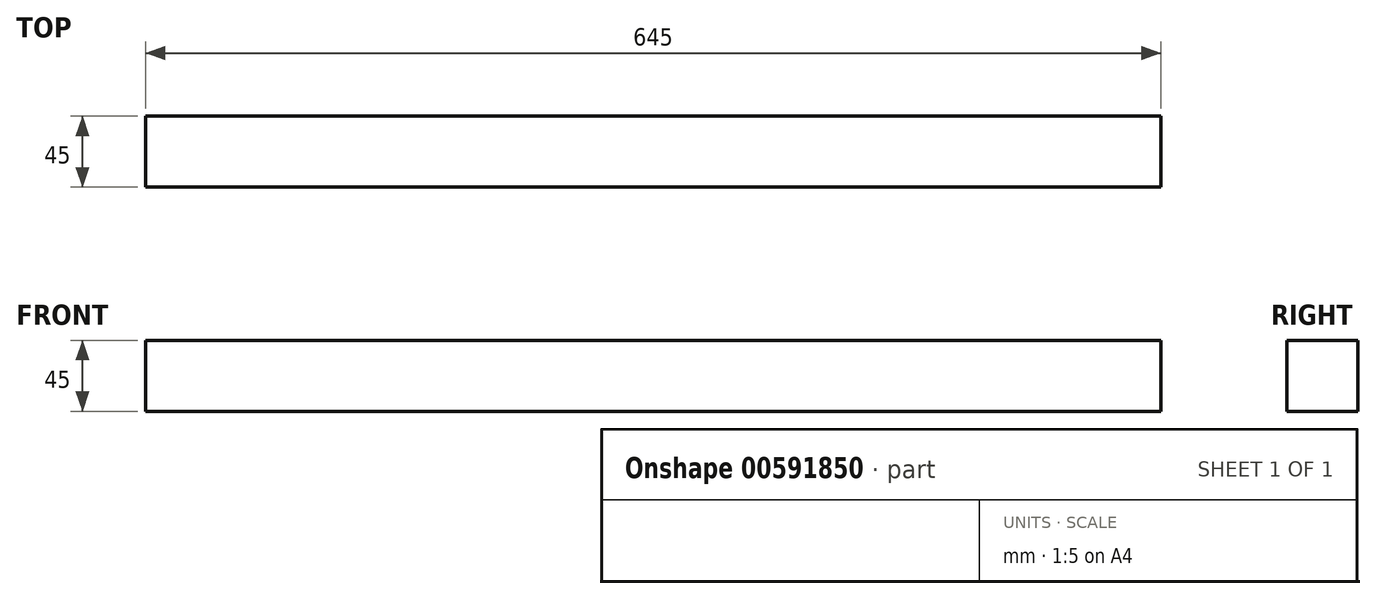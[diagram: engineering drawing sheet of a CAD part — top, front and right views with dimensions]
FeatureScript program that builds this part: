
annotation { "Feature Type Name" : "Feature", "Feature Type Description" : "" }
export const myFeature = defineFeature(function(context is Context, id is Id, definition is map)
    precondition{}
    {
        {
            var Q0;
            Q0=qCreatedBy(makeId("Right.planeOp"),FACE);
            var sketch = newSketch(context, id + "F0", { "sketchPlane" : qUnion([Q0])});
            skLineSegment(sketch, "E0.bottom", {"start": v(0, 0) * mm, "end": v(45, 0) * mm});
            skLineSegment(sketch, "E0.top", {"start": v(0, 45) * mm, "end": v(45, 45) * mm});
            skLineSegment(sketch, "E0.left", {"start": v(0, 0) * mm, "end": v(0, 45) * mm});
            skLineSegment(sketch, "E0.right", {"start": v(45, 0) * mm, "end": v(45, 45) * mm});
            skSolve(sketch);
        }
        {
            var Q0;
            Q0=makeQuery(id+"F0.imprint","IMPRINT",FACE,{"disambiguationData":[TD([[makeQuery(id+"F0.imprint","IMPRINT",EDGE,{"derivedFrom":sQuery(id+"F0.wireOp",EDGE,"E0.bottom")}),1.0]])]});
            extrude(context, id + "F1", {"entities" : qUnion([Q0]), "depth" : 645 * mm, "offsetDistance" : 25 * mm});
        }
    });
